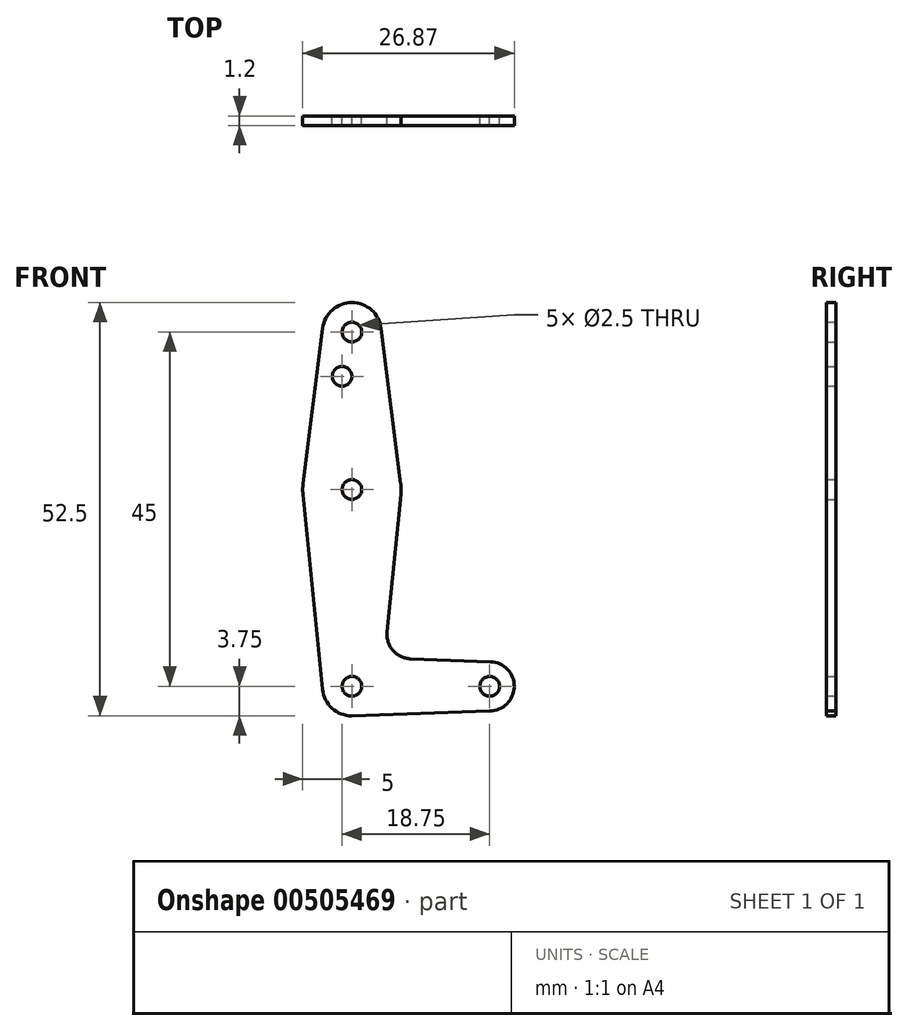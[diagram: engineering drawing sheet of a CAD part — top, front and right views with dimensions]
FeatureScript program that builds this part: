
annotation { "Feature Type Name" : "Feature", "Feature Type Description" : "" }
export const myFeature = defineFeature(function(context is Context, id is Id, definition is map)
    precondition{}
    {
        {
            var Q0;
            Q0=qCreatedBy(makeId("Front.planeOp"),FACE);
            var sketch = newSketch(context, id + "F0", { "sketchPlane" : qUnion([Q0])});
            skLineSegment(sketch, "E0", {"start": v(0, 0) * mm, "end": v(0, 45) * mm, "construction": true});
            skLineSegment(sketch, "E1", {"start": v(0, 0) * mm, "end": v(17.5, 0) * mm, "construction": true});
            skCircle(sketch, "E2", {"center": v(0, 0) * mm, "radius": 3.75 * mm});
            skCircle(sketch, "E3", {"center": v(17.5, 0) * mm, "radius": 3.12 * mm});
            skCircle(sketch, "E4", {"center": v(0, 45) * mm, "radius": 3.75 * mm});
            skCircle(sketch, "E5", {"center": v(0, 25) * mm, "radius": 6.25 * mm});
            skLineSegment(sketch, "E6", {"start": v(0, -3.75) * mm, "end": v(17.5, -3.13) * mm});
            skCircle(sketch, "E7", {"center": v(0, 45) * mm, "radius": 1.25 * mm});
            skCircle(sketch, "E8", {"center": v(0, 25) * mm, "radius": 1.25 * mm});
            skCircle(sketch, "E9", {"center": v(0, 0) * mm, "radius": 1.25 * mm});
            skCircle(sketch, "E10", {"center": v(17.5, 0) * mm, "radius": 1.25 * mm});
            skCircle(sketch, "E11", {"center": v(-1.25, 39.38) * mm, "radius": 1.25 * mm});
            skPoint(sketch, "E12.newPointA", {"position": v(0, 3.75) * mm});
            skLineSegment(sketch, "E13", {"start": v(4.47, 6.93) * mm, "end": v(6.22, 24.38) * mm});
            skLineSegment(sketch, "E14", {"start": v(-6.22, 24.38) * mm, "end": v(-3.73, -0.38) * mm});
            skLineSegment(sketch, "E15", {"start": v(-6.2, 25.78) * mm, "end": v(-3.72, 45.47) * mm});
            skLineSegment(sketch, "E16", {"start": v(3.72, 45.47) * mm, "end": v(6.2, 25.78) * mm});
            skLineSegment(sketch, "E17", {"start": v(7.47, 3.49) * mm, "end": v(17.61, 3.12) * mm});
            skArc(sketch, "E18.filletArc", {"start": v(4.47, 6.93) * mm, "mid": v(5.22, 4.56) * mm, "end": v(7.47, 3.49) * mm});
            skSolve(sketch);
        }
        {
            var Q0;
            {var subQ0=sQuery(id+"F0.wireOp",EDGE,"E13");Q0=makeQuery(id+"F0.imprint","IMPRINT",FACE,{"disambiguationData":[TD([[makeQuery(id+"F0.imprint","IMPRINT",EDGE,{"derivedFrom":subQ0}),1.0]])]});}
            var Q1;
            Q1=makeQuery(id+"F0.imprint","IMPRINT",FACE,{"disambiguationData":[TD([[makeQuery(id+"F0.imprint","IMPRINT",EDGE,{"derivedFrom":sQuery(id+"F0.wireOp",EDGE,"E11")}),-1.0]])]});
            var Q2;
            Q2=makeQuery(id+"F0.imprint","IMPRINT",FACE,{"disambiguationData":[TD([[makeQuery(id+"F0.imprint","IMPRINT",EDGE,{"derivedFrom":sQuery(id+"F0.wireOp",EDGE,"E8")}),-1.0]])]});
            var Q3;
            Q3=makeQuery(id+"F0.imprint","IMPRINT",FACE,{"disambiguationData":[TD([[makeQuery(id+"F0.imprint","IMPRINT",EDGE,{"derivedFrom":sQuery(id+"F0.wireOp",EDGE,"E7")}),-1.0]])]});
            var Q4;
            Q4=makeQuery(id+"F0.imprint","IMPRINT",FACE,{"disambiguationData":[TD([[makeQuery(id+"F0.imprint","IMPRINT",EDGE,{"derivedFrom":sQuery(id+"F0.wireOp",EDGE,"E9")}),-1.0]])]});
            var Q5;
            Q5=makeQuery(id+"F0.imprint","IMPRINT",FACE,{"disambiguationData":[TD([[makeQuery(id+"F0.imprint","IMPRINT",EDGE,{"derivedFrom":sQuery(id+"F0.wireOp",EDGE,"E10")}),-1.0]])]});
            extrude(context, id + "F1", {"entities" : qUnion([Q0, Q1, Q2, Q3, Q4, Q5]), "depth" : 1.2 * mm});
        }
    });
